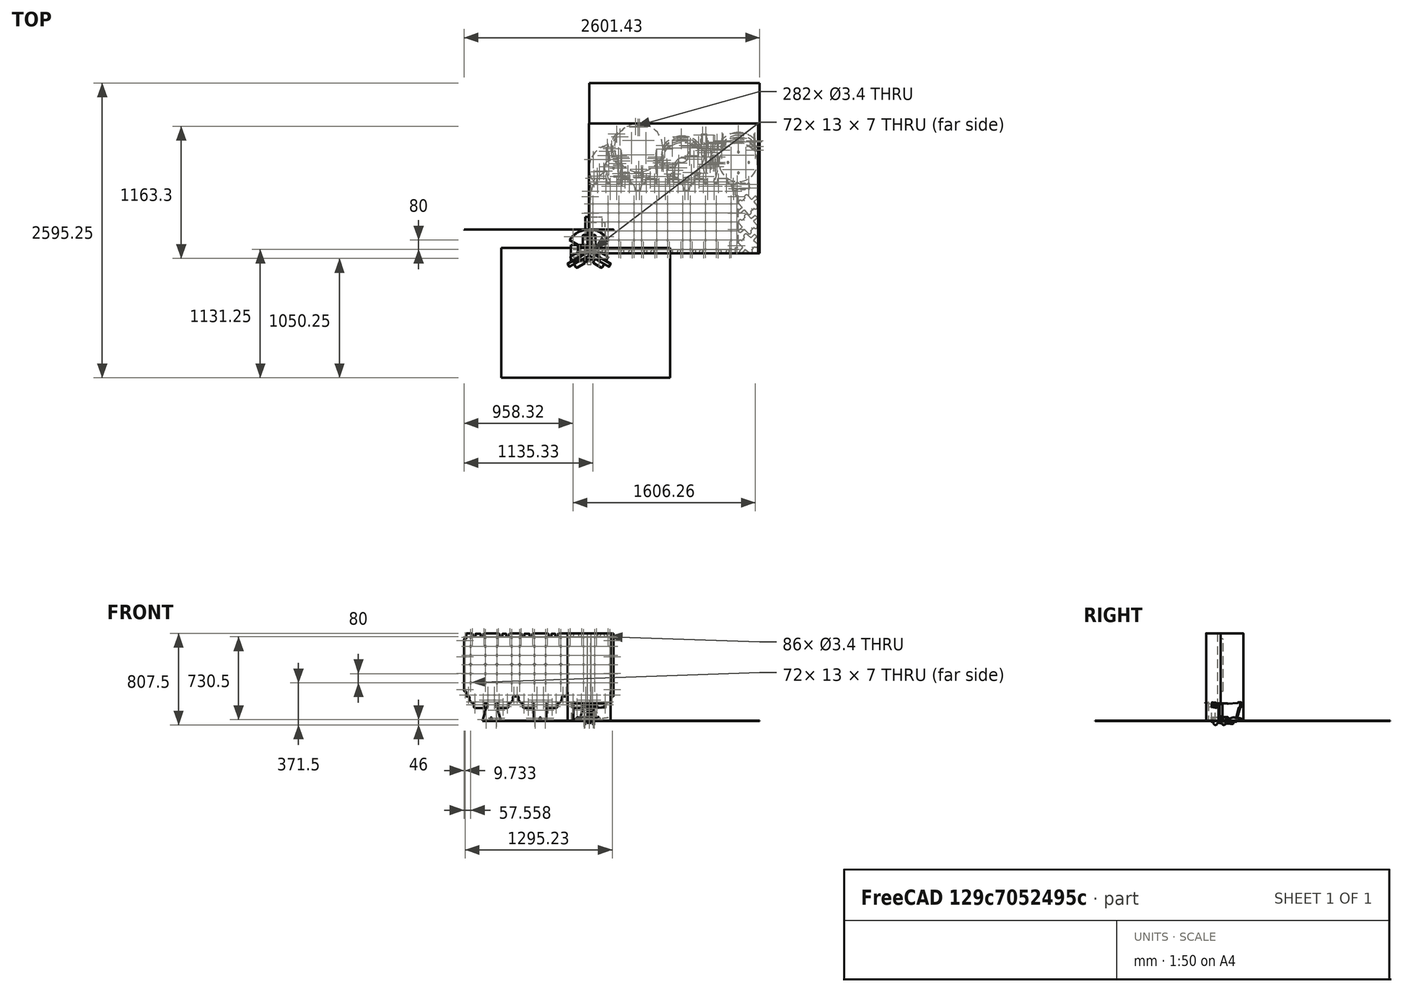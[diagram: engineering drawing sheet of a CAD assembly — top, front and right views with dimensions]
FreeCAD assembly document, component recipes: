
FREECAD ASSEMBLY — COMPONENT RECIPES ("composit_stand_small_3")

This assembly document has 19 components, labeled P0..P18 below (a component is one placed body or linked part). 18 of them carry a construction recipe — the FreeCAD feature program that regenerates the part from scratch, quoted from this document or its linked companion documents; the rest are supplied as boundary geometry only. No exploded tour is included for this assembly.
NOTE — document 2 of 2 of this assembly tour. The two overview renders and the header above are repeated from document 1; the component sections below continue where the previous document stopped.
COMPONENT P17 — recipe-attached ("ugol_mini_material_0.30ansi", modeled in this document).
Construction recipe (the document's own serialized feature program — sketch geometry with constraints, then the solid features built on it; lengths are millimeters unless a unit is written):

FEATURE [PartDesign::CoordinateSystem] LCS_0005
  AttacherType = Attacher::AttachEngine3D
  MapMode = 2
  Support = -> [X_Axis035]
FEATURE [Sketcher::SketchObject] Sketch104
  FullyConstrained = false
  MapMode = 5
  Placement = pos=(0,0,0) rot=(0.57735,0.57735,0.57735;2.0944rad)
  Support = -> [YZ_Plane035]
  expr: Constraints[6] = 2mm + 0.5mm + 3.4mm + 2mm + 3mm
  sketch-geometry (3):
    g0: LineSegment StartX=10.9 StartY=0 StartZ=0 EndX=0 EndY=0 EndZ=0
    g1: LineSegment StartX=0 StartY=0 StartZ=0 EndX=0 EndY=17.2 EndZ=0
    g2: GeomPoint X=12.5 Y=0 Z=0
  constraints (7):
    c: PointOnObject(g0,g-1)
    c: Coincident(g0,g-1)
    c: Coincident(g0,g1)
    c: PointOnObject(g1,g-2)
    c: PointOnObject(g2,g-1)
    c: DistanceY(g1) = 17.2
    c: DistanceX(g0,g0) = 10.9
FEATURE [PartDesign::FeaturePython] BaseBend006  # WARN: FeaturePython — macro-defined, semantics opaque (R4)
  BendSide = 0
  BendSketch = -> Sketch104
  MidPlane = true
  Reverse = false
  length = 9.4
  radius = 2
  thickness = 0.5
  expr: length = <<main>>.rivet_d + 6mm
FEATURE [Sketcher::SketchObject] Sketch105
  AttachmentOffset = pos=(0,5.9,0) rot=(0,0,1;0rad)
  FullyConstrained = true
  MapMode = 5
  Placement = pos=(0,5.9,0) rot=(0,0,1;0rad)
  Support = -> [XY_Plane036]
  expr: .AttachmentOffset.Base.y = 2mm + 0.5mm + 2mm + 1.4mm
  expr: Constraints[1] = <<main>>.rivet_d
  sketch-geometry (1):
    g0: Circle CenterX=0 CenterY=0 CenterZ=0 NormalX=0 NormalY=0 NormalZ=1 AngleXU=0 Radius=1.7
  constraints (2):
    c: Coincident(g0,g-1)
    c: Diameter(g0) = 3.4
FEATURE [PartDesign::Plane] DatumPlane024
  AttachmentOffset = pos=(0,0,0) rot=(1,0,0;0.785398rad)
  Length = 61.8921
  MapMode = 5
  Placement = pos=(0,0,0) rot=(1,0,0;0.785398rad)
  ResizeMode = 0
  Support = -> [XY_Plane036]
  Width = 82.6027
FEATURE [PartDesign::Fillet] Fillet002
  Base = -> BaseBend006 [Edge25,Edge8]
  BaseFeature = -> BaseBend006
  Radius = 2
  SupportTransform = false
  UseAllEdges = false
FEATURE [PartDesign::Mirrored] Mirrored038
  BaseFeature = -> Fillet002
  MirrorPlane = -> YZ_Plane035
  Originals = -> [Fillet002]
FEATURE [PartDesign::Pocket] Pocket061
  BaseFeature = -> Mirrored038
  Direction = (0,0,-1)
  Length = 5
  Length2 = 5
  Midplane = true
  Profile = -> Sketch105
  ReferenceAxis = -> Sketch105 [N_Axis]
  Type = 1
FEATURE [Sketcher::SketchObject] Sketch106
  AttachmentOffset = pos=(0,12.5,0) rot=(0,0,1;0rad)
  FullyConstrained = true
  MapMode = 5
  Placement = pos=(0,-2.8e-15,12.5) rot=(1,0,0;1.5708rad)
  Support = -> [XZ_Plane035]
  expr: .AttachmentOffset.Base.y = 12.5mm
  expr: Constraints[1] = <<main>>.rivet_d
  sketch-geometry (1):
    g0: Circle CenterX=0 CenterY=0 CenterZ=0 NormalX=0 NormalY=0 NormalZ=1 AngleXU=0 Radius=1.7
  constraints (2):
    c: Coincident(g0,g-1)
    c: Diameter(g0) = 3.4
FEATURE [PartDesign::Pocket] Pocket062
  BaseFeature = -> Pocket061
  Direction = (0,1,2e-16)
  Length = 5
  Length2 = 5
  Midplane = true
  Profile = -> Sketch106
  ReferenceAxis = -> Sketch106 [N_Axis]
  Type = 1
FEATURE [PartDesign::Body] Body_7  label="ugol_mini_material_0.30ansi"
  Group = -> [LCS_0005,Sketch104,BaseBend006,Sketch105,DatumPlane024,Fillet002,Mirrored038,Pocket061,Sketch106,Pocket062]
  Origin = -> Origin035
  Tip = -> Pocket062
COMPONENT P18 — recipe-attached ("cover_bended_material_0.30ansi", modeled in this document).
Construction recipe (the document's own serialized feature program — sketch geometry with constraints, then the solid features built on it; lengths are millimeters unless a unit is written):

FEATURE [PartDesign::CoordinateSystem] LCS_0008
  AttacherType = Attacher::AttachEngine3D
  MapMode = 2
  Support = -> [X_Axis044]
FEATURE [Sketcher::SketchObject] Sketch138
  FullyConstrained = true
  MapMode = 5
  Support = -> [XY_Plane045]
  expr: Constraints[16] = Sketch003.Constraints.max_r
  expr: Constraints[17] = <<main>>.end_face_width / 2
  sketch-geometry (6):
    g0: LineSegment StartX=0 StartY=0 StartZ=0 EndX=181.736 EndY=104.925 EndZ=0
    g1: LineSegment StartX=0 StartY=39.9875 StartZ=0 EndX=1 EndY=39.9875 EndZ=0
    g2: LineSegment StartX=0 StartY=209.848 StartZ=0 EndX=1 EndY=209.848 EndZ=0
    g3: ArcOfCircle CenterX=0 CenterY=0 CenterZ=0 NormalX=0 NormalY=0 NormalZ=1 AngleXU=0 Radius=40 StartAngle=0.935116 EndAngle=1.54579
    g4: ArcOfCircle CenterX=0 CenterY=0 CenterZ=0 NormalX=0 NormalY=0 NormalZ=1 AngleXU=0 Radius=209.851 StartAngle=0.599917 EndAngle=1.56603
    g5: LineSegment StartX=23.749 StartY=32.1867 StartZ=0 EndX=173.207 EndY=118.476 EndZ=0
  constraints (19):
    c: Coincident(g0,g-1)
    c: Angle(g-1,g0) = 0.523599
    c: PointOnObject(g1,g-2)
    c: Horizontal(g1)
    c: PointOnObject(g2,g-2)
    c: Horizontal(g2)
    c: Vertical(g2,g1)
    c: DistanceX(g1) = 1
    c: Coincident(g3,g0)
    c: Coincident(g3,g1)
    c: Coincident(g4,g3)
    c: Coincident(g4,g2)
    c: Coincident(g5,g3)
    c: Coincident(g5,g4)
    c: Parallel(g5,g0)
    c: PointOnObject(g0,g4)
    c: DistanceY(g2) = 209.848
    c: Distance(g4,g0) = 16
    c: Diameter(g3) = 80
FEATURE [PartDesign::CoordinateSystem] Local_CS047
  AttacherType = Attacher::AttachEngine3D
  AttachmentOffset = pos=(0,0,0) rot=(-1,0,0;0.087266rad)
  MapMode = 5
  Placement = pos=(0,0,0) rot=(-1,0,0;0.087266rad)
  Support = -> [XY_Plane045]
FEATURE [PartDesign::CoordinateSystem] Local_CS048
  AttacherType = Attacher::AttachEngine3D
  AttachmentOffset = pos=(0,0,0) rot=(0.043053,-0.160675,0.986068;0.530656rad)
  MapMode = 5
  Placement = pos=(0,0,0) rot=(0.043053,-0.160675,0.986068;0.530656rad)
  Support = -> [XY_Plane045]
FEATURE [PartDesign::Line] DatumLine
  AttacherType = Attacher::AttachEngineLine
  Length = 20
  MapMode = 16
  Placement = pos=(0,0,0) rot=(0.363387,0.629406,0.686876;2.3865rad)
  ResizeMode = 0
  Support = -> [Local_CS048]
FEATURE [PartDesign::CoordinateSystem] Local_CS049
  AttacherType = Attacher::AttachEngine3D
  AttachmentOffset = pos=(0,0,0) rot=(0,0,-1;0.523599rad)
  MapMode = 5
  Placement = pos=(0,0,0) rot=(0.5,-0.866025,0;0.087266rad)
  Support = -> [Local_CS048]
FEATURE [Sketcher::SketchObject] Sketch139
  AttachmentOffset = pos=(0,0,0) rot=(1,0,0;1.5708rad)
  FullyConstrained = true
  MapMode = 5
  Placement = pos=(0,0,0) rot=(0.998634,-0.036953,0.036953;1.61582rad)
  Support = -> [Local_CS049]
  expr: Constraints[3] = <<main>>.cover_bend_mid
  sketch-geometry (2):
    g0: LineSegment StartX=0 StartY=0 StartZ=0 EndX=400 EndY=34.9955 EndZ=0
    g1: LineSegment StartX=0 StartY=0 StartZ=0 EndX=-400 EndY=34.9955 EndZ=0
  constraints (5):
    c: Coincident(g0,g-1)
    c: Coincident(g1,g0)
    c: Symmetric(g0,g1,g-2)
    c: Angle(g-1,g0) = 0.0872665
    c: DistanceX(g0) = 400
FEATURE [PartDesign::FeaturePython] BaseBend010  # WARN: FeaturePython — macro-defined, semantics opaque (R4)
  BendSide = 0
  BendSketch = -> Sketch139
  MidPlane = false
  Reverse = true
  length = 500
  radius = 0.1
  thickness = 0.3
FEATURE [Sketcher::SketchObject] Sketch140
  AttachmentOffset = pos=(0,0,0) rot=(0,1,0;-0.087266rad)
  ExternalGeometry = -> [Sketch138]
  FullyConstrained = false
  MapMode = 5
  Placement = pos=(0,0,0) rot=(-0.258803,0.965864,0.0113;6.1146rad)
  Support = -> [Local_CS049]
  sketch-geometry (14):
    g0: LineSegment StartX=23.2598 StartY=32.117 StartZ=0 EndX=170.272 EndY=118.078 EndZ=0
    g1: ArcOfEllipse CenterX=1 CenterY=7.19572 CenterZ=0 NormalX=0 NormalY=0 NormalZ=1 MajorRadius=202.441 MinorRadius=202.319 AngleXU=-1.5708 StartAngle=2.15044 EndAngle=3.14159
    g2: LineSegment StartX=1 StartY=-195.245 StartZ=0 EndX=1 EndY=209.636 EndZ=0
    g3: LineSegment StartX=203.319 StartY=7.19572 StartZ=0 EndX=-201.319 EndY=7.19572 EndZ=0
    g4: GeomPoint X=1 Y=0.187598 Z=0
    g5: GeomPoint X=1 Y=14.2038 Z=0
    g6: LineSegment StartX=0 StartY=209.636 StartZ=0 EndX=1 EndY=209.636 EndZ=0
    g7: LineSegment StartX=0 StartY=39.0768 StartZ=0 EndX=1 EndY=39.0768 EndZ=0
    g8: ArcOfCircle CenterX=1 CenterY=0 CenterZ=0 NormalX=0 NormalY=0 NormalZ=1 AngleXU=0 Radius=39.0768 StartAngle=0.964726 EndAngle=1.5708
    g9: LineSegment StartX=0 StartY=-278.705 StartZ=0 EndX=616.451 EndY=-278.705 EndZ=0
    g10: LineSegment StartX=616.451 StartY=-278.705 StartZ=0 EndX=616.451 EndY=663.316 EndZ=0
    g11: LineSegment StartX=616.451 StartY=663.316 StartZ=0 EndX=0 EndY=663.316 EndZ=0
    g12: LineSegment StartX=0 StartY=663.316 StartZ=0 EndX=0 EndY=209.636 EndZ=0
    g13: LineSegment StartX=0 StartY=39.0768 StartZ=0 EndX=0 EndY=-278.705 EndZ=0
  constraints (27):
    c: Coincident(g0,g-3)
    c: Coincident(g0,g-3)
    c: InternalAlignment(g2-g5 -> g1) x4
    c: Horizontal(g3)
    c: Coincident(g1,g0)
    c: PointOnObject(g6,g-2)
    c: Horizontal(g6)
    c: Tangent(g1,g6) = 1.5708
    c: PointOnObject(g7,g-2)
    c: Horizontal(g7)
    c: Coincident(g8,g0)
    c: Tangent(g7,g8) = 1.5708
    c: Vertical(g7,g1)
    c: DistanceX(g1) = 1
    c: PointOnObject(g1,g-4)
    c: Horizontal(g8,g-4)
    c: Coincident(g9,g10)
    c: Coincident(g10,g11)
    c: Coincident(g11,g12)
    c: Coincident(g13,g9)
    c: Horizontal(g9)
    c: Horizontal(g11)
    c: Vertical(g10)
    c: Vertical(g12)
    c: PointOnObject(g9,g-2)
    c: Coincident(g13,g7)
    c: Coincident(g12,g6)
FEATURE [Sketcher::SketchObject] Sketch141
  AttachmentOffset = pos=(0,0,0) rot=(1,0,0;-0.087266rad)
  ExternalGeometry = -> [Sketch140]
  FullyConstrained = false
  MapMode = 5
  Placement = pos=(0,0,0) rot=(1,0,0;6.19592rad)
  Support = -> [XY_Plane045]
  sketch-geometry (10):
    g0: LineSegment StartX=-0.5 StartY=38.7427 StartZ=0 EndX=-0.5 EndY=0 EndZ=0
    g1: LineSegment StartX=-0.5 StartY=0 StartZ=0 EndX=0.5 EndY=0 EndZ=0
    g2: LineSegment StartX=0.5 StartY=0 StartZ=0 EndX=0.5 EndY=38.7427 EndZ=0
    g3: LineSegment StartX=0.5 StartY=38.7427 StartZ=0 EndX=-0.5 EndY=38.7427 EndZ=0
    g4: GeomPoint X=0 Y=19.3713 Z=0
    g5: LineSegment StartX=-0.5 StartY=207.844 StartZ=0 EndX=-0.5 EndY=768.027 EndZ=0
    g6: LineSegment StartX=-0.5 StartY=768.027 StartZ=0 EndX=0.5 EndY=768.027 EndZ=0
    g7: LineSegment StartX=0.5 StartY=768.027 StartZ=0 EndX=0.5 EndY=207.844 EndZ=0
    g8: LineSegment StartX=0.5 StartY=207.844 StartZ=0 EndX=-0.5 EndY=207.844 EndZ=0
    g9: GeomPoint X=0 Y=487.936 Z=0
  constraints (25):
    c: Coincident(g0,g1)
    c: Coincident(g1,g2)
    c: Coincident(g2,g3)
    c: Coincident(g3,g0)
    c: Horizontal(g1)
    c: Horizontal(g3)
    c: Vertical(g0)
    c: Vertical(g2)
    c: Symmetric(g1,g0,g4)
    c: PointOnObject(g4,g-2)
    c: PointOnObject(g1,g-1)
    c: Coincident(g5,g6)
    c: Coincident(g6,g7)
    c: Coincident(g7,g8)
    c: Coincident(g8,g5)
    c: Horizontal(g6)
    c: Horizontal(g8)
    c: Vertical(g5)
    c: Vertical(g7)
    c: Symmetric(g6,g5,g9)
    c: PointOnObject(g9,g-2)
    c: DistanceX(g6,g6) = 1
    c: DistanceX(g3,g3) = 1
    c: PointOnObject(g-4,g8)
    c: PointOnObject(g-3,g3)
FEATURE [PartDesign::Pocket] Pocket096
  BaseFeature = -> BaseBend010
  Direction = (0,-0.0871557,-0.996195)
  Length = 5
  Length2 = 5
  Midplane = true
  Profile = -> Sketch141
  ReferenceAxis = -> Sketch141 [N_Axis]
  Refine = true
  Type = 1
FEATURE [PartDesign::Pocket] Pocket095
  BaseFeature = -> Pocket096
  Direction = (0.162099,0.0432684,-0.985825)
  Length = 5
  Length2 = 5
  Midplane = true
  Profile = -> Sketch140
  ReferenceAxis = -> Sketch140 [N_Axis]
  Type = 1
FEATURE [PartDesign::Mirrored] Mirrored041
  BaseFeature = -> Pocket095
  MirrorPlane = -> YZ_Plane044
  Originals = -> [Pocket095]
  Refine = true
FEATURE [PartDesign::Body] cover_bender  label="cover_bended_material_0.30ansi"
  Group = -> [LCS_0008,Sketch138,Sketch139,BaseBend010,Local_CS047,Pocket096,Sketch140,Pocket095,Mirrored041,Sketch141,Local_CS048,DatumLine,Local_CS049]
  Origin = -> Origin044
  Tip = -> Mirrored041
PROVENANCE & LICENSES
A FreeCAD (.FCStd) document from a public repository crawl; recipes are the document's own serialized feature recipes (and, for linked parts, companion documents' recipes).
License: as declared in the source repository (recorded in the dataset sidecar).
